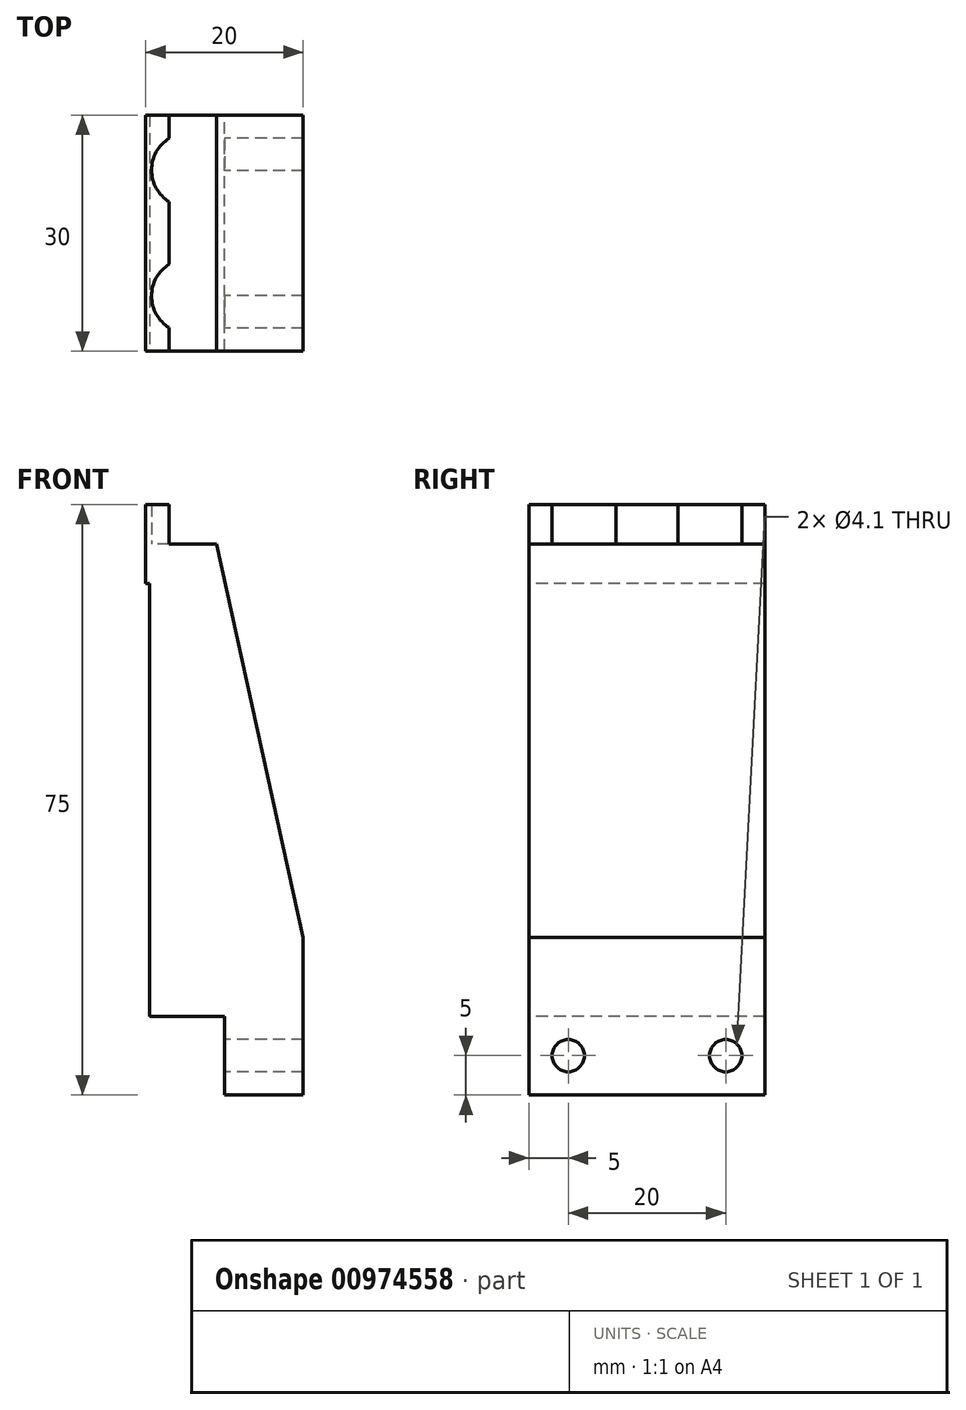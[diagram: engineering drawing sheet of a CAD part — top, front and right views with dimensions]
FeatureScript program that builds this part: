
annotation { "Feature Type Name" : "Feature", "Feature Type Description" : "" }
export const myFeature = defineFeature(function(context is Context, id is Id, definition is map)
    precondition{}
    {
        {
            var Q0;
            Q0=qCreatedBy(makeId("Front.planeOp"),FACE);
            var sketch = newSketch(context, id + "F0", { "sketchPlane" : qUnion([Q0])});
            skLineSegment(sketch, "E0.bottom", {"start": v(0, 0) * mm, "end": v(-20, 0) * mm});
            skLineSegment(sketch, "E0.top", {"start": v(0, 70) * mm, "end": v(-20, 70) * mm});
            skLineSegment(sketch, "E0.left", {"start": v(0, 0) * mm, "end": v(0, 70) * mm});
            skLineSegment(sketch, "E0.right", {"start": v(-20, 0) * mm, "end": v(-20, 70) * mm});
            skSolve(sketch);
        }
        {
            var Q0;
            Q0=makeQuery(id+"F0.imprint","IMPRINT",FACE,{"disambiguationData":[TD([[makeQuery(id+"F0.imprint","IMPRINT",EDGE,{"derivedFrom":sQuery(id+"F0.wireOp",EDGE,"E0.bottom")}),-1.0]])]});
            extrude(context, id + "F1", {"entities" : qUnion([Q0]), "depth" : 30 * mm});
        }
        {
            var Q0;
            Q0=makeQuery(id+"F1.opExtrude","SWEPT_FACE",FACE,{"disambiguationData":[OSD([sQuery(id+"F0.wireOp",EDGE,"E0.right")])]});
            var sketch = newSketch(context, id + "F2", { "sketchPlane" : qUnion([Q0])});
            skLineSegment(sketch, "E1.bottom", {"start": v(0, 0) * mm, "end": v(30, 0) * mm});
            skLineSegment(sketch, "E1.top", {"start": v(0, 10) * mm, "end": v(30, 10) * mm});
            skLineSegment(sketch, "E1.left", {"start": v(0, 0) * mm, "end": v(0, 10) * mm});
            skLineSegment(sketch, "E1.right", {"start": v(30, 0) * mm, "end": v(30, 10) * mm});
            skSolve(sketch);
        }
        {
            var Q0;
            Q0=qSketchRegion(id+"F2",true);
            extrude(context, id + "F3", {"entities" : qUnion([Q0]), "operationType" : NewBodyOperationType.REMOVE, "oppositeDirection" : true, "depth" : 10 * mm});
        }
        {
            var Q0;
            Q0=makeQuery(id+"F3.boolean.opBoolean","COPY",FACE,{"derivedFrom":makeQuery(id+"F3.opExtrude","CAP_FACE",FACE,{"disambiguationData":[OSD([sQuery(id+"F2.wireOp",EDGE,"E1.bottom"),sQuery(id+"F2.wireOp",EDGE,"E1.top"),sQuery(id+"F2.wireOp",EDGE,"E1.left"),sQuery(id+"F2.wireOp",EDGE,"E1.right")])],"isStart":false})});
            var sketch = newSketch(context, id + "F4", { "sketchPlane" : qUnion([Q0])});
            skCircle(sketch, "E2", {"center": v(5, 5) * mm, "radius": 2.05 * mm});
            skCircle(sketch, "E3", {"center": v(25, 5) * mm, "radius": 2.05 * mm});
            skSolve(sketch);
        }
        {
            var Q0;
            Q0=qSketchRegion(id+"F4",true);
            extrude(context, id + "F5", {"entities" : qUnion([Q0]), "operationType" : NewBodyOperationType.REMOVE, "endBound" : BoundingType.UP_TO_NEXT, "oppositeDirection" : true, "depth" : 25 * mm});
        }
        {
            var Q0;
            Q0=makeQuery(id+"F1.opExtrude","SWEPT_FACE",FACE,{"disambiguationData":[OSD([sQuery(id+"F0.wireOp",EDGE,"E0.top")])]});
            var sketch = newSketch(context, id + "F6", { "sketchPlane" : qUnion([Q0])});
            skLineSegment(sketch, "E4.bottom", {"start": v(0, 0) * mm, "end": v(-11, 0) * mm});
            skLineSegment(sketch, "E4.top", {"start": v(0, -30) * mm, "end": v(-11, -30) * mm});
            skLineSegment(sketch, "E4.left", {"start": v(0, 0) * mm, "end": v(0, -30) * mm});
            skLineSegment(sketch, "E4.right", {"start": v(-11, 0) * mm, "end": v(-11, -30) * mm});
            skSolve(sketch);
        }
        {
            var Q0;
            Q0=qSketchRegion(id+"F6",true);
            extrude(context, id + "F7", {"entities" : qUnion([Q0]), "operationType" : NewBodyOperationType.REMOVE, "oppositeDirection" : true, "depth" : 50 * mm});
        }
        {
            var Q0;
            Q0=makeQuery(id+"F1.opExtrude","SWEPT_FACE",FACE,{"disambiguationData":[OSD([sQuery(id+"F0.wireOp",EDGE,"E0.top")])]});
            var sketch = newSketch(context, id + "F8", { "sketchPlane" : qUnion([Q0])});
            skLineSegment(sketch, "E5", {"start": v(-37.78, -15) * mm, "end": v(17.7, -15) * mm, "construction": true});
            skLineSegment(sketch, "E6", {"start": v(-30.22, -7) * mm, "end": v(11.91, -7) * mm, "construction": true});
            skLineSegment(sketch, "E7", {"start": v(-33.53, -23) * mm, "end": v(14.63, -23) * mm, "construction": true});
            skLineSegment(sketch, "E8", {"start": v(-14.5, 4.82) * mm, "end": v(-14.5, -41.88) * mm, "construction": true});
            skArc(sketch, "E9", {"start": v(-17, -2.96) * mm, "mid": v(-19.25, -7) * mm, "end": v(-17, -11.04) * mm, "construction": true});
            skArc(sketch, "E10", {"start": v(-17, -18.96) * mm, "mid": v(-19.25, -23) * mm, "end": v(-17, -27.04) * mm, "construction": true});
            skLineSegment(sketch, "E11", {"start": v(-17, 19.13) * mm, "end": v(-17, -11.04) * mm, "construction": true});
            skLineSegment(sketch, "E12", {"start": v(-17, -2.96) * mm, "end": v(-17, 0) * mm});
            skLineSegment(sketch, "E13", {"start": v(-17, 0) * mm, "end": v(-20, 0) * mm});
            skLineSegment(sketch, "E14", {"start": v(-20, 0) * mm, "end": v(-20, -30) * mm});
            skLineSegment(sketch, "E15", {"start": v(-20, -30) * mm, "end": v(-17, -30) * mm});
            skLineSegment(sketch, "E16", {"start": v(-17, -30) * mm, "end": v(-17, -27.04) * mm});
            skLineSegment(sketch, "E17", {"start": v(-17, -18.96) * mm, "end": v(-17, -11.04) * mm});
            skPoint(sketch, "E18", {"position": v(-19.25, -7) * mm});
            skPoint(sketch, "E19", {"position": v(-19.25, -23) * mm});
            skArc(sketch, "E20", {"start": v(-17, -2.96) * mm, "mid": v(-19.25, -7) * mm, "end": v(-17, -11.04) * mm});
            skArc(sketch, "E21", {"start": v(-17, -18.96) * mm, "mid": v(-19.25, -23) * mm, "end": v(-17, -27.04) * mm});
            skLineSegment(sketch, "E22", {"start": v(-17, -11.04) * mm, "end": v(-17, -48.69) * mm, "construction": true});
            skSolve(sketch);
        }
        {
            var Q0;
            Q0=qSketchRegion(id+"F8",true);
            extrude(context, id + "F9", {"entities" : qUnion([Q0]), "operationType" : NewBodyOperationType.ADD, "depth" : 5 * mm});
        }
        {
            var Q0;
            Q0=makeQuery(id+"F7.boolean.opBoolean","COPY",EDGE,{"derivedFrom":makeQuery(id+"F7.opExtrude","CAP_EDGE",EDGE,{"disambiguationData":[OSD([sQuery(id+"F6.wireOp",EDGE,"E4.right")])],"isStart":false})});
            chamfer(context, id + "F10", {"entities" : qUnion([Q0]), "chamferType" : ChamferType.TWO_OFFSETS, "width1" : 11 * mm, "oppositeDirection" : false, "width2" : 50 * mm, "tangentPropagation" : true});
        }
        {
            var Q0;
            Q0=makeQuery(id+"F9.boolean.opBoolean","MERGE",FACE,{"derivedFrom":[makeQuery(id+"F1.opExtrude","SWEPT_FACE",FACE,{"disambiguationData":[OSD([sQuery(id+"F0.wireOp",EDGE,"E0.right")])]}),makeQuery(id+"F9.opExtrude","SWEPT_FACE",FACE,{"disambiguationData":[OSD([sQuery(id+"F8.wireOp",EDGE,"E14")])]})]});
            var sketch = newSketch(context, id + "F11", { "sketchPlane" : qUnion([Q0])});
            skLineSegment(sketch, "E23.bottom", {"start": v(0, 10) * mm, "end": v(30, 10) * mm});
            skLineSegment(sketch, "E23.top", {"start": v(0, 65) * mm, "end": v(30, 65) * mm});
            skLineSegment(sketch, "E23.left", {"start": v(0, 10) * mm, "end": v(0, 65) * mm});
            skLineSegment(sketch, "E23.right", {"start": v(30, 10) * mm, "end": v(30, 65) * mm});
            skSolve(sketch);
        }
        {
            var Q0;
            Q0 = qSketchRegion(id + "F11", true);
            extrude(context, id + "F12", {"entities" : qUnion([Q0]), "operationType" : NewBodyOperationType.REMOVE, "oppositeDirection" : true, "depth" : 0.5 * mm, "offsetDistance" : 25 * mm});
        }
    });
